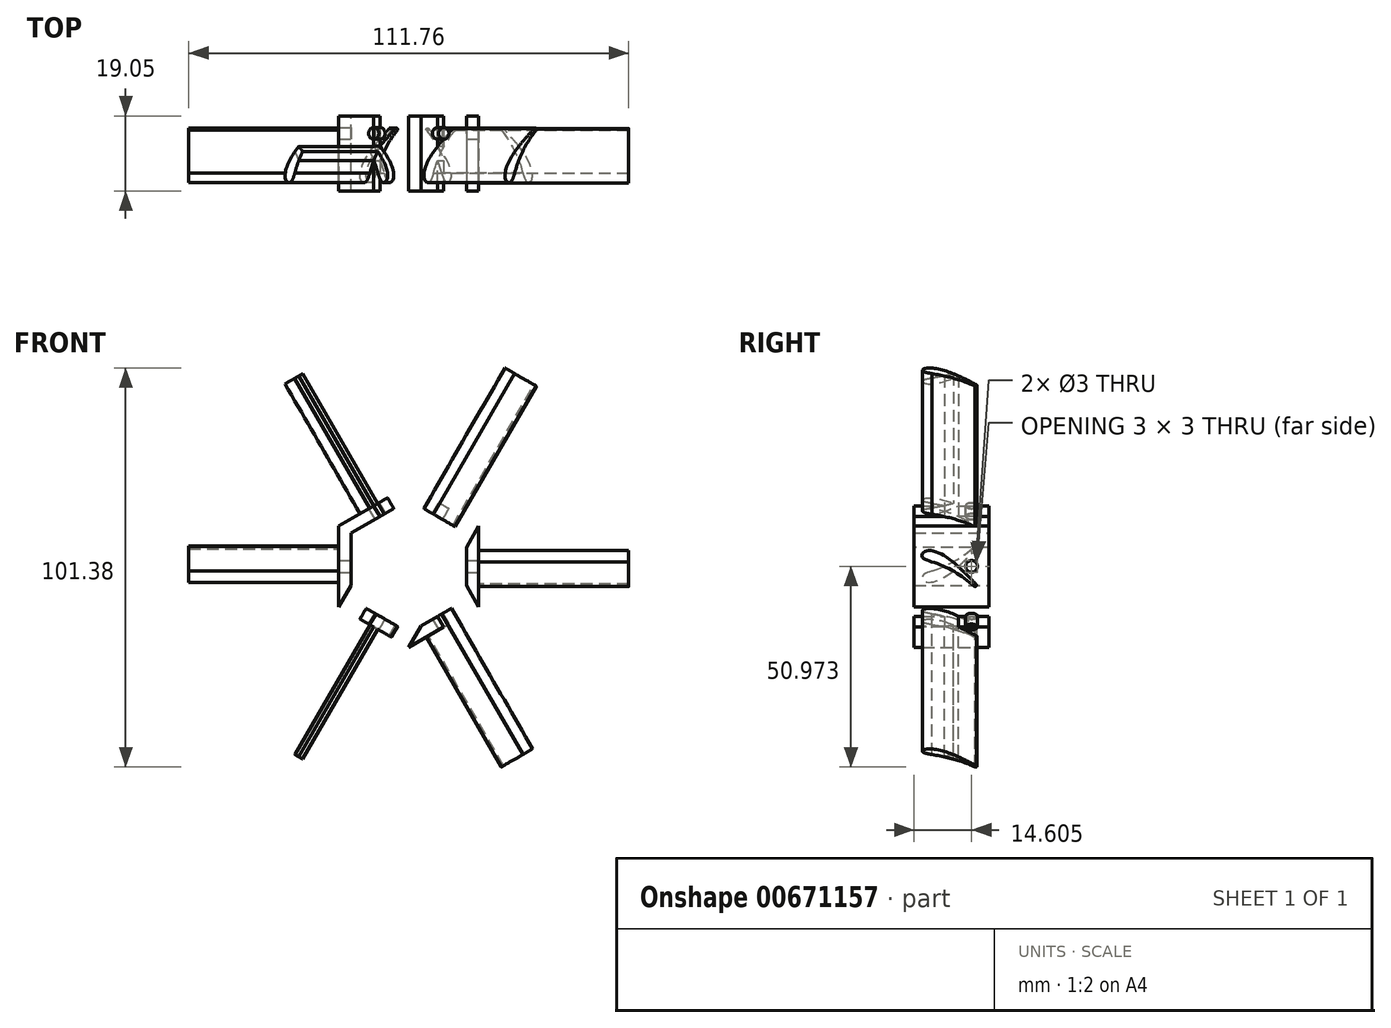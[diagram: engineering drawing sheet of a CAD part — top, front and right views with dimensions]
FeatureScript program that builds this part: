
annotation { "Feature Type Name" : "Feature", "Feature Type Description" : "" }
export const myFeature = defineFeature(function(context is Context, id is Id, definition is map)
    precondition{}
    {
        {
            var Q0;
            Q0=qCreatedBy(makeId("Front.planeOp"),FACE);
            var sketch = newSketch(context, id + "F0", { "sketchPlane" : qUnion([Q0])});
            skCircle(sketch, "E0.cCircle", {"center": v(0, 0) * mm, "radius": 17.78 * mm, "construction": true});
            skLineSegment(sketch, "E0.0", {"start": v(17.78, 10.27) * mm, "end": v(17.78, -10.27) * mm});
            skLineSegment(sketch, "E0.1", {"start": v(17.78, -10.27) * mm, "end": v(0, -20.53) * mm});
            skLineSegment(sketch, "E0.2", {"start": v(0, -20.53) * mm, "end": v(-17.78, -10.27) * mm});
            skLineSegment(sketch, "E0.3", {"start": v(-17.78, -10.27) * mm, "end": v(-17.78, 10.27) * mm});
            skLineSegment(sketch, "E0.4", {"start": v(-17.78, 10.27) * mm, "end": v(0, 20.53) * mm});
            skLineSegment(sketch, "E0.5", {"start": v(0, 20.53) * mm, "end": v(17.78, 10.27) * mm});
            skPoint(sketch, "E0.0.midPoint", {"position": v(17.78, 0) * mm});
            skSolve(sketch);
        }
        {
            var Q0;
            Q0=makeQuery(id+"F0.imprint","IMPRINT",FACE,{"disambiguationData":[TD([[makeQuery(id+"F0.imprint","IMPRINT",EDGE,{"derivedFrom":sQuery(id+"F0.wireOp",EDGE,"E0.0")}),-1.0]])]});
            extrude(context, id + "F1", {"entities" : qUnion([Q0]), "depth" : 19.05 * mm, "offsetDistance" : 25.4 * mm});
        }
        {
            var Q0;
            Q0=makeQuery(id+"F1.opExtrude","SWEPT_FACE",FACE,{"disambiguationData":[OSD([sQuery(id+"F0.wireOp",EDGE,"E0.5")])]});
            var sketch = newSketch(context, id + "F2", { "sketchPlane" : qUnion([Q0])});
            skLineSegment(sketch, "E1", {"start": v(0, 0) * mm, "end": v(0, -19.05) * mm});
            skPoint(sketch, "E2", {"position": v(0, -9.53) * mm});
            skFitSpline(sketch, "E3", {"points": [v(-1.19, -14.5) * mm, v(-2.57, -16.9) * mm, v(-3.83, -16.16) * mm, v(-2.94, -11.66) * mm, v(4.47, -3.26) * mm], "startDerivative": vector(-5.87, -16.48) * mm, "endDerivative": vector(22.04, 21.13) * mm});
            skArc(sketch, "E4", {"start": v(5.1, -3.62) * mm, "mid": v(1.33, -8.7) * mm, "end": v(-1.19, -14.5) * mm});
            skArc(sketch, "E5", {"start": v(5.1, -3.62) * mm, "mid": v(4.97, -3.12) * mm, "end": v(4.47, -3.26) * mm});
            skLineSegment(sketch, "E6", {"start": v(0, 0) * mm, "end": v(0, -4.45) * mm});
            skCircle(sketch, "E7", {"center": v(0, -4.45) * mm, "radius": 1.5 * mm});
            skSolve(sketch);
        }
        {
            var Q0;
            Q0=makeQuery(id+"F1.opExtrude","SWEPT_FACE",FACE,{"disambiguationData":[OSD([sQuery(id+"F0.wireOp",EDGE,"E0.0")])]});
            var sketch = newSketch(context, id + "F3", { "sketchPlane" : qUnion([Q0])});
            skLineSegment(sketch, "E8", {"start": v(0, 0) * mm, "end": v(-19.05, 0) * mm});
            skLineSegment(sketch, "E9", {"start": v(0.25, 0) * mm, "end": v(-18.8, 0) * mm});
            skFitSpline(sketch, "E10", {"points": [v(-14.64, 1.2) * mm, v(-17.02, 2.57) * mm, v(-16.3, 3.84) * mm, v(-11.79, 2.95) * mm, v(-3.39, -4.47) * mm], "startDerivative": vector(-16.48, 5.87) * mm, "endDerivative": vector(21.13, -22.04) * mm});
            skArc(sketch, "E11", {"start": v(-3.75, -5.1) * mm, "mid": v(-8.83, -1.33) * mm, "end": v(-14.64, 1.2) * mm});
            skArc(sketch, "E12", {"start": v(-3.75, -5.1) * mm, "mid": v(-3.25, -4.97) * mm, "end": v(-3.39, -4.47) * mm});
            skLineSegment(sketch, "E13", {"start": v(0, 0) * mm, "end": v(-4.44, 0) * mm});
            skCircle(sketch, "E14", {"center": v(-4.44, 0) * mm, "radius": 1.5 * mm});
            skSolve(sketch);
        }
        {
            var Q0;
            Q0=makeQuery(id+"F1.opExtrude","SWEPT_FACE",FACE,{"disambiguationData":[OSD([sQuery(id+"F0.wireOp",EDGE,"E0.1")])]});
            var sketch = newSketch(context, id + "F4", { "sketchPlane" : qUnion([Q0])});
            skLineSegment(sketch, "E15", {"start": v(0, 0) * mm, "end": v(0, 19.05) * mm});
            skLineSegment(sketch, "E16", {"start": v(0, 0) * mm, "end": v(0, 19.04) * mm});
            skFitSpline(sketch, "E17", {"points": [v(1.2, 14.5) * mm, v(2.57, 16.88) * mm, v(3.84, 16.15) * mm, v(2.95, 11.65) * mm, v(-4.46, 3.25) * mm], "startDerivative": vector(5.87, 16.48) * mm, "endDerivative": vector(-22.04, -21.13) * mm});
            skArc(sketch, "E18", {"start": v(-5.1, 3.61) * mm, "mid": v(-1.33, 8.7) * mm, "end": v(1.2, 14.5) * mm});
            skArc(sketch, "E19", {"start": v(-5.1, 3.61) * mm, "mid": v(-4.97, 3.11) * mm, "end": v(-4.46, 3.25) * mm});
            skLineSegment(sketch, "E20", {"start": v(0, 0) * mm, "end": v(0, 4.44) * mm});
            skCircle(sketch, "E21", {"center": v(0, 4.44) * mm, "radius": 1.5 * mm});
            skSolve(sketch);
        }
        {
            var Q0;
            Q0=makeQuery(id+"F1.opExtrude","SWEPT_FACE",FACE,{"disambiguationData":[OSD([sQuery(id+"F0.wireOp",EDGE,"E0.2")])]});
            var sketch = newSketch(context, id + "F5", { "sketchPlane" : qUnion([Q0])});
            skLineSegment(sketch, "E22", {"start": v(0, 0) * mm, "end": v(0, 19.05) * mm});
            skLineSegment(sketch, "E23", {"start": v(0, 0.04) * mm, "end": v(0, 19.09) * mm});
            skFitSpline(sketch, "E24", {"points": [v(1.18, 14.54) * mm, v(2.56, 16.93) * mm, v(3.83, 16.2) * mm, v(2.94, 11.7) * mm, v(-4.47, 3.3) * mm], "startDerivative": vector(5.87, 16.48) * mm, "endDerivative": vector(-22.04, -21.13) * mm});
            skArc(sketch, "E25", {"start": v(-5.11, 3.66) * mm, "mid": v(-1.34, 8.74) * mm, "end": v(1.18, 14.54) * mm});
            skArc(sketch, "E26", {"start": v(-5.11, 3.66) * mm, "mid": v(-4.98, 3.16) * mm, "end": v(-4.47, 3.3) * mm});
            skSolve(sketch);
        }
        {
            var Q0;
            Q0=makeQuery(id+"F1.opExtrude","SWEPT_FACE",FACE,{"disambiguationData":[OSD([sQuery(id+"F0.wireOp",EDGE,"E0.3")])]});
            var sketch = newSketch(context, id + "F6", { "sketchPlane" : qUnion([Q0])});
            skLineSegment(sketch, "E27", {"start": v(0, 0) * mm, "end": v(19.05, 0) * mm});
            skLineSegment(sketch, "E28", {"start": v(0.03, 0) * mm, "end": v(19.08, 0) * mm});
            skFitSpline(sketch, "E29", {"points": [v(14.53, -1.19) * mm, v(16.92, -2.57) * mm, v(16.19, -3.83) * mm, v(11.68, -2.94) * mm, v(3.28, 4.47) * mm], "startDerivative": vector(16.48, -5.87) * mm, "endDerivative": vector(-21.13, 22.04) * mm});
            skArc(sketch, "E30", {"start": v(3.65, 5.1) * mm, "mid": v(8.73, 1.33) * mm, "end": v(14.53, -1.19) * mm});
            skArc(sketch, "E31", {"start": v(3.65, 5.1) * mm, "mid": v(3.15, 4.97) * mm, "end": v(3.28, 4.47) * mm});
            skSolve(sketch);
        }
        {
            var Q0;
            Q0=makeQuery(id+"F1.opExtrude","SWEPT_FACE",FACE,{"disambiguationData":[OSD([sQuery(id+"F0.wireOp",EDGE,"E0.4")])]});
            var sketch = newSketch(context, id + "F7", { "sketchPlane" : qUnion([Q0])});
            skLineSegment(sketch, "E32", {"start": v(0, 0) * mm, "end": v(0, -19.05) * mm});
            skLineSegment(sketch, "E33", {"start": v(0, -0.02) * mm, "end": v(0, -19.07) * mm});
            skFitSpline(sketch, "E34", {"points": [v(-1.19, -14.52) * mm, v(-2.57, -16.91) * mm, v(-3.83, -16.18) * mm, v(-2.94, -11.68) * mm, v(4.47, -3.28) * mm], "startDerivative": vector(-5.87, -16.48) * mm, "endDerivative": vector(22.04, 21.13) * mm});
            skArc(sketch, "E35", {"start": v(5.1, -3.64) * mm, "mid": v(1.33, -8.72) * mm, "end": v(-1.19, -14.52) * mm});
            skArc(sketch, "E36", {"start": v(5.1, -3.64) * mm, "mid": v(4.97, -3.14) * mm, "end": v(4.47, -3.28) * mm});
            skSolve(sketch);
        }
        {
            var Q0;
            {var subQ0=sQuery(id+"F7.wireOp",EDGE,"E34");var subQ1=sQuery(id+"F7.wireOp",EDGE,"E32");var subQ2=makeQuery(id+"F7.imprint","INTERSECT",VERTEX,{"derivedFrom":[subQ1,subQ0]});Q0=makeQuery(id+"F7.imprint","IMPRINT",FACE,{"disambiguationData":[TD([[makeQuery(id+"F7.imprint","IMPRINT",EDGE,{"disambiguationData":[TD([[subQ2,-1.0]])],"derivedFrom":subQ1}),-1.0]])]});}
            var Q1;
            {var subQ5=sQuery(id+"F7.wireOp",EDGE,"E36");Q1=makeQuery(id+"F7.imprint","IMPRINT",FACE,{"disambiguationData":[TD([[makeQuery(id+"F7.imprint","IMPRINT",EDGE,{"derivedFrom":subQ5}),1.0]])]});}
            extrude(context, id + "F8", {"entities" : qUnion([Q0, Q1]), "operationType" : NewBodyOperationType.ADD, "depth" : 38.1 * mm, "offsetDistance" : 25.4 * mm});
        }
        {
            var Q0;
            {var subQ0=sQuery(id+"F2.wireOp",EDGE,"E3");var subQ1=sQuery(id+"F2.wireOp",EDGE,"E1");var subQ2=makeQuery(id+"F2.imprint","INTERSECT",VERTEX,{"derivedFrom":[subQ1,subQ0]});Q0=makeQuery(id+"F2.imprint","IMPRINT",FACE,{"disambiguationData":[TD([[makeQuery(id+"F2.imprint","IMPRINT",EDGE,{"disambiguationData":[TD([[subQ2,-1.0]])],"derivedFrom":subQ1}),-1.0]])]});}
            var Q1;
            {var subQ5=sQuery(id+"F2.wireOp",EDGE,"E5");Q1=makeQuery(id+"F2.imprint","IMPRINT",FACE,{"disambiguationData":[TD([[makeQuery(id+"F2.imprint","IMPRINT",EDGE,{"derivedFrom":subQ5}),1.0]])]});}
            extrude(context, id + "F9", {"entities" : qUnion([Q0, Q1]), "operationType" : NewBodyOperationType.ADD, "depth" : 38.1 * mm, "offsetDistance" : 25.4 * mm});
        }
        {
            var Q0;
            {var subQ0=sQuery(id+"F3.wireOp",EDGE,"E10");var subQ1=sQuery(id+"F3.wireOp",EDGE,"E9");var subQ2=makeQuery(id+"F3.imprint","INTERSECT",VERTEX,{"derivedFrom":[subQ1,subQ0]});Q0=makeQuery(id+"F3.imprint","IMPRINT",FACE,{"disambiguationData":[TD([[makeQuery(id+"F3.imprint","IMPRINT",EDGE,{"disambiguationData":[TD([[subQ2,-1.0]])],"derivedFrom":subQ1}),-1.0]])]});}
            var Q1;
            {var subQ5=sQuery(id+"F3.wireOp",EDGE,"E12");Q1=makeQuery(id+"F3.imprint","IMPRINT",FACE,{"disambiguationData":[TD([[makeQuery(id+"F3.imprint","IMPRINT",EDGE,{"derivedFrom":subQ5}),1.0]])]});}
            extrude(context, id + "F10", {"entities" : qUnion([Q0, Q1]), "operationType" : NewBodyOperationType.ADD, "depth" : 38.1 * mm, "offsetDistance" : 25.4 * mm});
        }
        {
            var Q0;
            {var subQ0=sQuery(id+"F4.wireOp",EDGE,"E18");var subQ1=sQuery(id+"F4.wireOp",EDGE,"E16");var subQ2=makeQuery(id+"F4.imprint","INTERSECT",VERTEX,{"derivedFrom":[subQ1,subQ0]});Q0=makeQuery(id+"F4.imprint","IMPRINT",FACE,{"disambiguationData":[TD([[makeQuery(id+"F4.imprint","IMPRINT",EDGE,{"disambiguationData":[TD([[subQ2,1.0]])],"derivedFrom":subQ1}),-1.0]])]});}
            var Q1;
            {var subQ5=sQuery(id+"F4.wireOp",EDGE,"E19");Q1=makeQuery(id+"F4.imprint","IMPRINT",FACE,{"disambiguationData":[TD([[makeQuery(id+"F4.imprint","IMPRINT",EDGE,{"derivedFrom":subQ5}),1.0]])]});}
            extrude(context, id + "F11", {"entities" : qUnion([Q0, Q1]), "operationType" : NewBodyOperationType.ADD, "depth" : 38.1 * mm, "offsetDistance" : 25.4 * mm});
        }
        {
            var Q0;
            {var subQ0=sQuery(id+"F5.wireOp",EDGE,"E24");var subQ1=sQuery(id+"F5.wireOp",EDGE,"E22");var subQ2=makeQuery(id+"F5.imprint","INTERSECT",VERTEX,{"derivedFrom":[subQ1,subQ0]});Q0=makeQuery(id+"F5.imprint","IMPRINT",FACE,{"disambiguationData":[TD([[makeQuery(id+"F5.imprint","IMPRINT",EDGE,{"disambiguationData":[TD([[subQ2,-1.0]])],"derivedFrom":subQ1}),-1.0]])]});}
            var Q1;
            {var subQ5=sQuery(id+"F5.wireOp",EDGE,"E26");Q1=makeQuery(id+"F5.imprint","IMPRINT",FACE,{"disambiguationData":[TD([[makeQuery(id+"F5.imprint","IMPRINT",EDGE,{"derivedFrom":subQ5}),1.0]])]});}
            extrude(context, id + "F12", {"entities" : qUnion([Q0, Q1]), "operationType" : NewBodyOperationType.ADD, "depth" : 38.1 * mm, "offsetDistance" : 25.4 * mm});
        }
        {
            var Q0;
            {var subQ0=sQuery(id+"F6.wireOp",EDGE,"E29");var subQ1=sQuery(id+"F6.wireOp",EDGE,"E27");var subQ2=makeQuery(id+"F6.imprint","INTERSECT",VERTEX,{"derivedFrom":[subQ1,subQ0]});Q0=makeQuery(id+"F6.imprint","IMPRINT",FACE,{"disambiguationData":[TD([[makeQuery(id+"F6.imprint","IMPRINT",EDGE,{"disambiguationData":[TD([[subQ2,-1.0]])],"derivedFrom":subQ1}),-1.0]])]});}
            var Q1;
            {var subQ5=sQuery(id+"F6.wireOp",EDGE,"E31");Q1=makeQuery(id+"F6.imprint","IMPRINT",FACE,{"disambiguationData":[TD([[makeQuery(id+"F6.imprint","IMPRINT",EDGE,{"derivedFrom":subQ5}),1.0]])]});}
            extrude(context, id + "F13", {"entities" : qUnion([Q0, Q1]), "operationType" : NewBodyOperationType.ADD, "depth" : 38.1 * mm, "offsetDistance" : 25.4 * mm});
        }
        {
            var Q0;
            Q0=makeQuery(id+"F1.opExtrude","CAP_FACE",FACE,{"disambiguationData":[OSD([sQuery(id+"F0.wireOp",EDGE,"E0.0"),sQuery(id+"F0.wireOp",EDGE,"E0.1"),sQuery(id+"F0.wireOp",EDGE,"E0.2"),sQuery(id+"F0.wireOp",EDGE,"E0.3"),sQuery(id+"F0.wireOp",EDGE,"E0.4"),sQuery(id+"F0.wireOp",EDGE,"E0.5")])],"isStart":true});
            var sketch = newSketch(context, id + "F14", { "sketchPlane" : qUnion([Q0])});
            skCircle(sketch, "E37.cCircle", {"center": v(0, 0) * mm, "radius": 14.64 * mm, "construction": true});
            skLineSegment(sketch, "E37.0", {"start": v(0, -16.9) * mm, "end": v(-14.64, -8.45) * mm});
            skLineSegment(sketch, "E37.1", {"start": v(-14.64, -8.45) * mm, "end": v(-14.64, 8.45) * mm});
            skLineSegment(sketch, "E37.2", {"start": v(-14.64, 8.45) * mm, "end": v(0, 16.9) * mm});
            skLineSegment(sketch, "E37.3", {"start": v(0, 16.9) * mm, "end": v(14.64, 8.45) * mm});
            skLineSegment(sketch, "E37.4", {"start": v(14.64, 8.45) * mm, "end": v(14.64, -8.45) * mm});
            skLineSegment(sketch, "E37.5", {"start": v(14.64, -8.45) * mm, "end": v(0, -16.9) * mm});
            skPoint(sketch, "E37.0.midPoint", {"position": v(-7.32, -12.68) * mm});
            skSolve(sketch);
        }
        {
            var Q0;
            Q0=makeQuery(id+"F14.imprint","IMPRINT",FACE,{"disambiguationData":[TD([[makeQuery(id+"F14.imprint","IMPRINT",EDGE,{"derivedFrom":sQuery(id+"F14.wireOp",EDGE,"E37.0")}),-1.0]])]});
            extrude(context, id + "F15", {"entities" : qUnion([Q0]), "operationType" : NewBodyOperationType.REMOVE, "endBound" : BoundingType.THROUGH_ALL, "oppositeDirection" : true, "depth" : 25.4 * mm, "offsetDistance" : 25.4 * mm});
        }
        {
            var Q0;
            {var subQ0=sQuery(id+"F2.wireOp",EDGE,"E6");var subQ1=sQuery(id+"F2.wireOp",EDGE,"E1");var subQ2=makeQuery(id+"F2.imprint","INTERSECT",VERTEX,{"derivedFrom":[subQ1,subQ0]});Q0=makeQuery(id+"F2.imprint","IMPRINT",FACE,{"disambiguationData":[TD([[makeQuery(id+"F2.imprint","IMPRINT",EDGE,{"disambiguationData":[TD([[subQ2,-1.0]])],"derivedFrom":subQ1}),1.0]])]});}
            var Q1;
            {var subQ0=sQuery(id+"F2.wireOp",EDGE,"E6");var subQ1=sQuery(id+"F2.wireOp",EDGE,"E1");var subQ2=makeQuery(id+"F2.imprint","INTERSECT",VERTEX,{"derivedFrom":[subQ1,subQ0]});Q1=makeQuery(id+"F2.imprint","IMPRINT",FACE,{"disambiguationData":[TD([[makeQuery(id+"F2.imprint","IMPRINT",EDGE,{"disambiguationData":[TD([[subQ2,-1.0]])],"derivedFrom":subQ1}),-1.0]])]});}
            extrude(context, id + "F16", {"entities" : qUnion([Q0, Q1]), "operationType" : NewBodyOperationType.REMOVE, "endBound" : BoundingType.THROUGH_ALL, "oppositeDirection" : true, "depth" : 25.4 * mm, "offsetDistance" : 25.4 * mm});
        }
        {
            var Q0;
            {var subQ0=sQuery(id+"F4.wireOp",EDGE,"E20");var subQ1=sQuery(id+"F4.wireOp",EDGE,"E16");var subQ2=makeQuery(id+"F4.imprint","INTERSECT",VERTEX,{"derivedFrom":[subQ1,subQ0]});Q0=makeQuery(id+"F4.imprint","IMPRINT",FACE,{"disambiguationData":[TD([[makeQuery(id+"F4.imprint","IMPRINT",EDGE,{"disambiguationData":[TD([[subQ2,-1.0]])],"derivedFrom":subQ1}),-1.0]])]});}
            var Q1;
            {var subQ0=sQuery(id+"F4.wireOp",EDGE,"E21");var subQ1=sQuery(id+"F4.wireOp",EDGE,"E15");var subQ2=makeQuery(id+"F4.imprint","INTERSECT",VERTEX,{"disambiguationData":[OD(0.0)],"derivedFrom":[subQ1,subQ0]});Q1=makeQuery(id+"F4.imprint","IMPRINT",FACE,{"disambiguationData":[TD([[makeQuery(id+"F4.imprint","IMPRINT",EDGE,{"disambiguationData":[TD([[subQ2,-1.0]])],"derivedFrom":subQ1}),1.0]])]});}
            extrude(context, id + "F17", {"entities" : qUnion([Q0, Q1]), "operationType" : NewBodyOperationType.REMOVE, "endBound" : BoundingType.THROUGH_ALL, "oppositeDirection" : true, "depth" : 25.4 * mm, "offsetDistance" : 25.4 * mm});
        }
        {
            var Q0;
            {var subQ0=sQuery(id+"F3.wireOp",EDGE,"E9");var subQ1=makeQuery(id+"F3.imprint","INTERSECT",VERTEX,{"derivedFrom":[subQ0,sQuery(id+"F3.wireOp",EDGE,"E13")]});Q0=makeQuery(id+"F3.imprint","IMPRINT",FACE,{"disambiguationData":[TD([[makeQuery(id+"F3.imprint","IMPRINT",EDGE,{"disambiguationData":[TD([[subQ1,1.0]])],"derivedFrom":subQ0}),-1.0]])]});}
            var Q1;
            {var subQ0=sQuery(id+"F3.wireOp",EDGE,"E14");var subQ1=sQuery(id+"F3.wireOp",EDGE,"E8");var subQ2=makeQuery(id+"F3.imprint","INTERSECT",VERTEX,{"disambiguationData":[OD(0.0)],"derivedFrom":[subQ1,subQ0]});Q1=makeQuery(id+"F3.imprint","IMPRINT",FACE,{"disambiguationData":[TD([[makeQuery(id+"F3.imprint","IMPRINT",EDGE,{"disambiguationData":[TD([[subQ2,-1.0]])],"derivedFrom":subQ1}),1.0]])]});}
            extrude(context, id + "F18", {"entities" : qUnion([Q0, Q1]), "operationType" : NewBodyOperationType.REMOVE, "endBound" : BoundingType.THROUGH_ALL, "oppositeDirection" : true, "depth" : 25.4 * mm, "offsetDistance" : 25.4 * mm});
        }
    });
